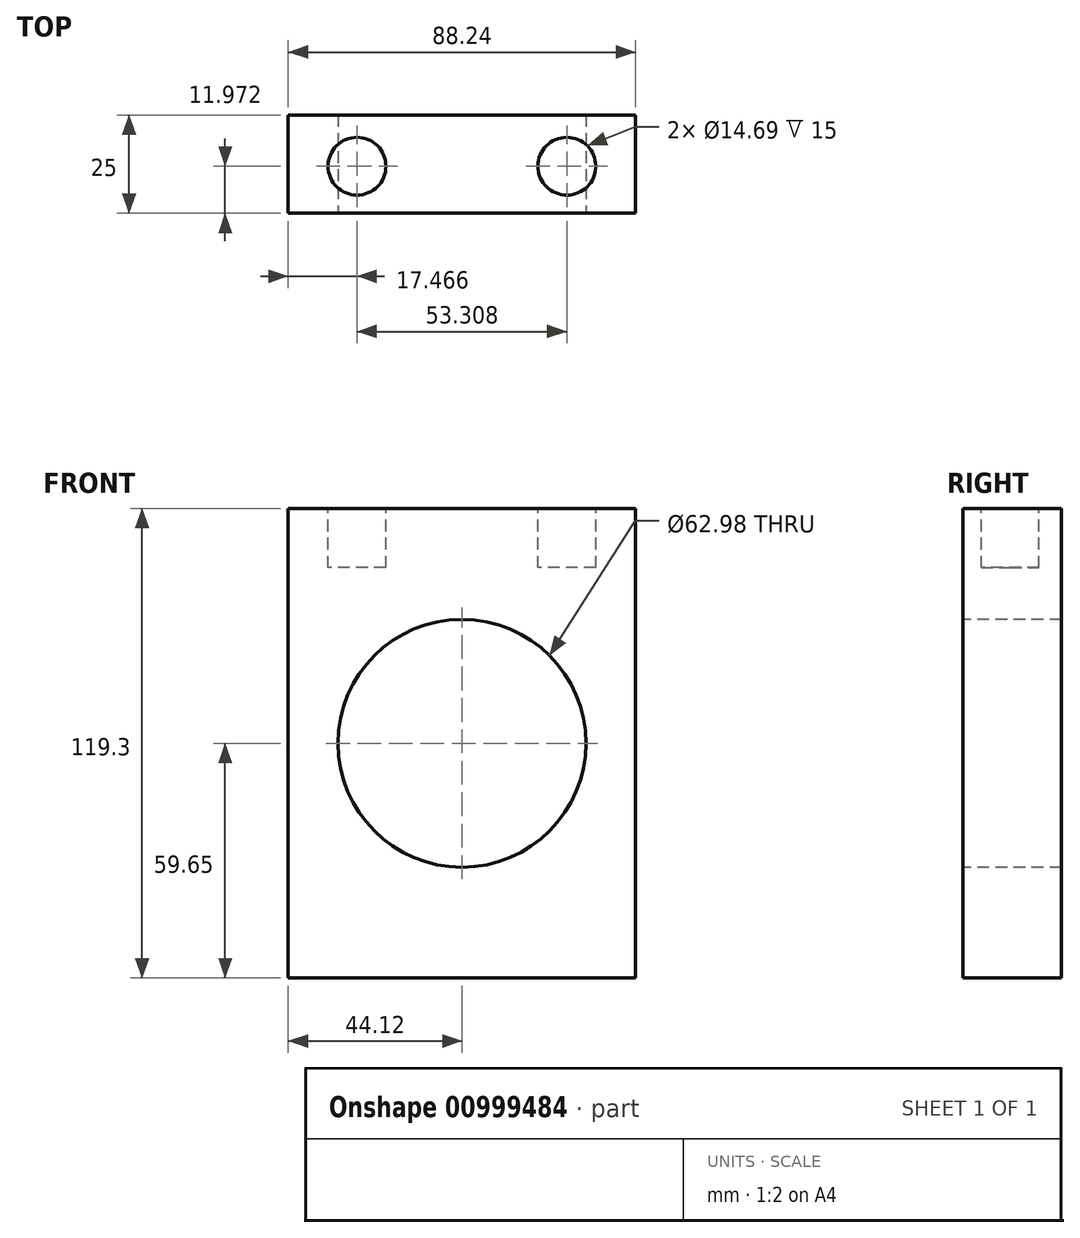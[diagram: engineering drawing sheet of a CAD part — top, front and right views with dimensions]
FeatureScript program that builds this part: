
annotation { "Feature Type Name" : "Feature", "Feature Type Description" : "" }
export const myFeature = defineFeature(function(context is Context, id is Id, definition is map)
    precondition{}
    {
        {
            var Q0;
            Q0=qCreatedBy(makeId("Front.planeOp"),FACE);
            var sketch = newSketch(context, id + "F0", { "sketchPlane" : qUnion([Q0])});
            skLineSegment(sketch, "E0.bottom", {"start": v(44.12, 59.65) * mm, "end": v(-44.12, 59.65) * mm});
            skLineSegment(sketch, "E0.top", {"start": v(44.12, -59.65) * mm, "end": v(-44.12, -59.65) * mm});
            skLineSegment(sketch, "E0.left", {"start": v(44.12, 59.65) * mm, "end": v(44.12, -59.65) * mm});
            skLineSegment(sketch, "E0.right", {"start": v(-44.12, 59.65) * mm, "end": v(-44.12, -59.65) * mm});
            skPoint(sketch, "E0.middle", {"position": v(0, 0) * mm});
            skSolve(sketch);
        }
        {
            var Q0;
            Q0 = qSketchRegion(id + "F0", true);
            extrude(context, id + "F1", {"entities" : qUnion([Q0]), "depth" : 25 * mm, "offsetDistance" : 25 * mm});
        }
        {
            var Q0;
            Q0=makeQuery(id+"F1.opExtrude","CAP_FACE",FACE,{"disambiguationData":[OSD([sQuery(id+"F0.wireOp",EDGE,"E0.bottom"),sQuery(id+"F0.wireOp",EDGE,"E0.top"),sQuery(id+"F0.wireOp",EDGE,"E0.left"),sQuery(id+"F0.wireOp",EDGE,"E0.right")])],"isStart":false});
            var sketch = newSketch(context, id + "F2", { "sketchPlane" : qUnion([Q0])});
            skCircle(sketch, "E1", {"center": v(0, 0) * mm, "radius": 31.5 * mm});
            skSolve(sketch);
        }
        {
            var Q0;
            Q0=makeQuery(id+"F1.opExtrude","SWEPT_FACE",FACE,{"disambiguationData":[OSD([sQuery(id+"F0.wireOp",EDGE,"E0.bottom")])]});
            var sketch = newSketch(context, id + "F3", { "sketchPlane" : qUnion([Q0])});
            skPoint(sketch, "E2.start.orphan", {"position": v(54.5, 0) * mm});
            skCircle(sketch, "E3", {"center": v(-26.65, -13.03) * mm, "radius": 7.34 * mm});
            skLineSegment(sketch, "E4", {"start": v(0, 0) * mm, "end": v(0, -25) * mm});
            skCircle(sketch, "E5.MirrorC", {"center": v(26.65, -13.03) * mm, "radius": 7.34 * mm});
            skSolve(sketch);
        }
        {
            var Q0;
            Q0 = qSketchRegion(id + "F3", true);
            extrude(context, id + "F4", {"entities" : qUnion([Q0]), "operationType" : NewBodyOperationType.REMOVE, "oppositeDirection" : true, "depth" : 15 * mm, "offsetDistance" : 25 * mm});
        }
        {
            var Q0;
            Q0=makeQuery(id+"F2.imprint","IMPRINT",FACE,{"disambiguationData":[TD([[makeQuery(id+"F2.imprint","IMPRINT",EDGE,{"derivedFrom":sQuery(id+"F2.wireOp",EDGE,"E1")}),1.0]])]});
            extrude(context, id + "F5", {"entities" : qUnion([Q0]), "operationType" : NewBodyOperationType.REMOVE, "endBound" : BoundingType.UP_TO_NEXT, "oppositeDirection" : true, "depth" : 25 * mm, "offsetDistance" : 25 * mm});
        }
    });
